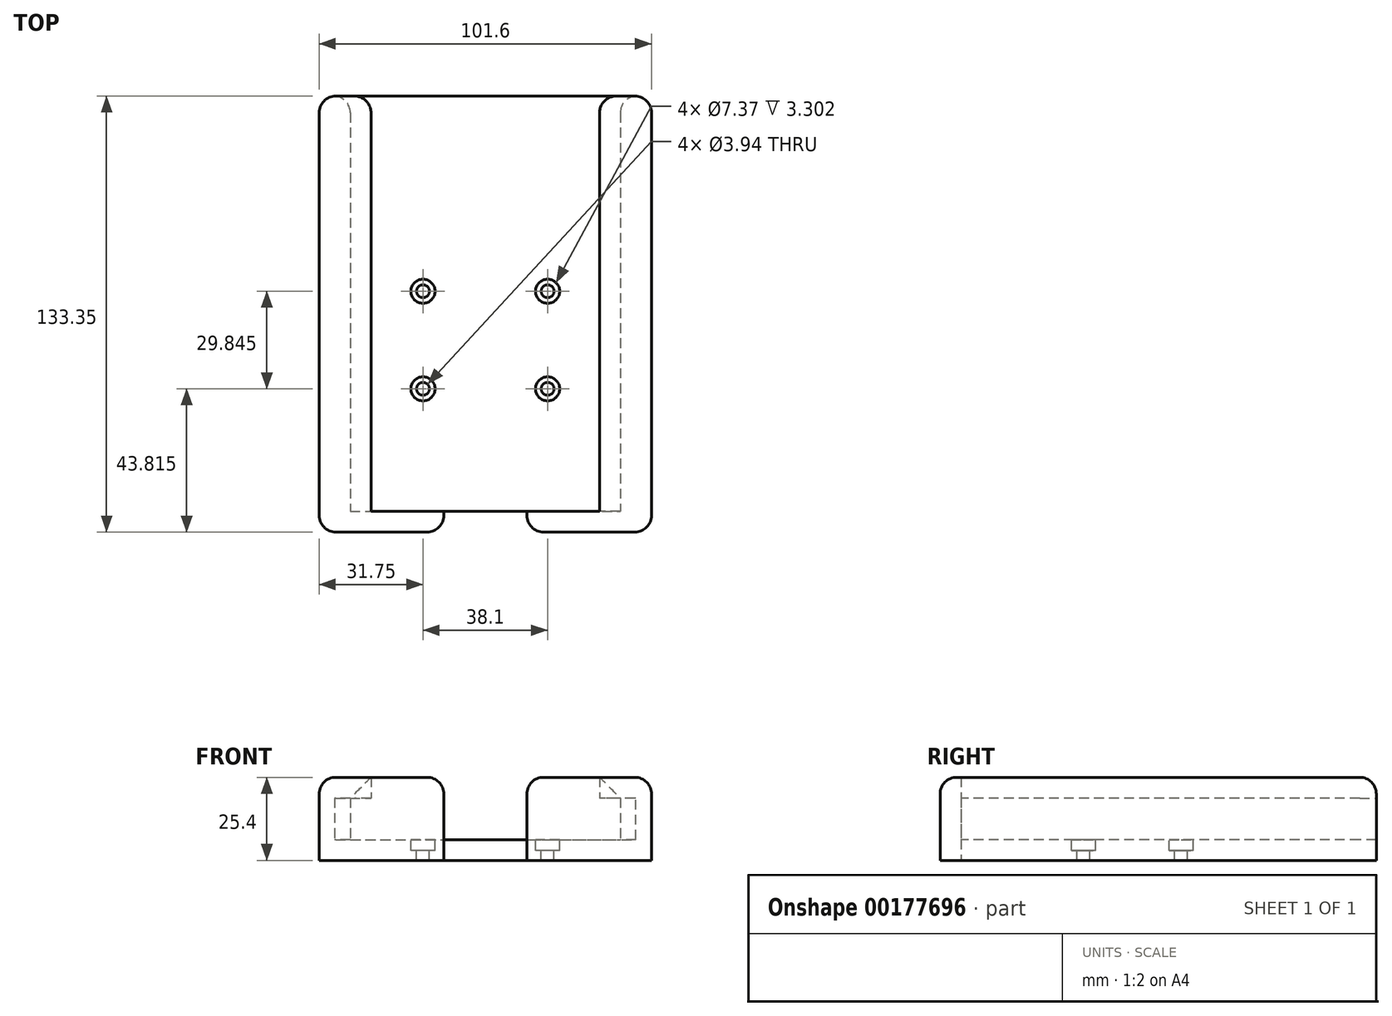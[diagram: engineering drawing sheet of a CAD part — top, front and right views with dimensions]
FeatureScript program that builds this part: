
annotation { "Feature Type Name" : "Feature", "Feature Type Description" : "" }
export const myFeature = defineFeature(function(context is Context, id is Id, definition is map)
    precondition{}
    {
        {
            var Q0;
            Q0=qCreatedBy(makeId("Top.planeOp"),FACE);
            var sketch = newSketch(context, id + "F0", { "sketchPlane" : qUnion([Q0])});
            skLineSegment(sketch, "E0.bottom", {"start": v(-50.8, 63.5) * mm, "end": v(50.8, 63.5) * mm});
            skLineSegment(sketch, "E0.top", {"start": v(-50.8, -63.5) * mm, "end": v(50.8, -63.5) * mm});
            skLineSegment(sketch, "E0.left", {"start": v(-50.8, 63.5) * mm, "end": v(-50.8, -63.5) * mm});
            skLineSegment(sketch, "E0.right", {"start": v(50.8, 63.5) * mm, "end": v(50.8, -63.5) * mm});
            skSolve(sketch);
        }
        {
            var Q0;
            Q0=makeQuery(id+"F0.imprint","IMPRINT",FACE,{"disambiguationData":[TD([[makeQuery(id+"F0.imprint","IMPRINT",EDGE,{"derivedFrom":sQuery(id+"F0.wireOp",EDGE,"E0.bottom")}),-1.0]])]});
            extrude(context, id + "F1", {"entities" : qUnion([Q0]), "depth" : 6.35 * mm});
        }
        {
            var Q0;
            Q0=makeQuery(id+"F1.opExtrude","CAP_FACE",FACE,{"disambiguationData":[OSD([sQuery(id+"F0.wireOp",EDGE,"E0.bottom"),sQuery(id+"F0.wireOp",EDGE,"E0.top"),sQuery(id+"F0.wireOp",EDGE,"E0.left"),sQuery(id+"F0.wireOp",EDGE,"E0.right")])],"isStart":false});
            var sketch = newSketch(context, id + "F2", { "sketchPlane" : qUnion([Q0])});
            skLineSegment(sketch, "E1.bottom", {"start": v(-50.8, 63.5) * mm, "end": v(-41.27, 63.5) * mm});
            skLineSegment(sketch, "E1.top", {"start": v(-50.8, -63.5) * mm, "end": v(-41.27, -63.5) * mm});
            skLineSegment(sketch, "E1.left", {"start": v(-50.8, 63.5) * mm, "end": v(-50.8, -63.5) * mm});
            skLineSegment(sketch, "E1.right", {"start": v(-41.27, 63.5) * mm, "end": v(-41.27, -63.5) * mm});
            skLineSegment(sketch, "E2.bottom", {"start": v(50.8, 63.5) * mm, "end": v(41.28, 63.5) * mm});
            skLineSegment(sketch, "E2.top", {"start": v(50.8, -63.5) * mm, "end": v(41.28, -63.5) * mm});
            skLineSegment(sketch, "E2.left", {"start": v(50.8, 63.5) * mm, "end": v(50.8, -63.5) * mm});
            skLineSegment(sketch, "E2.right", {"start": v(41.28, 63.5) * mm, "end": v(41.28, -63.5) * mm});
            skSolve(sketch);
        }
        {
            var Q0;
            Q0=makeQuery(id+"F2.imprint","IMPRINT",FACE,{"disambiguationData":[TD([[makeQuery(id+"F2.imprint","IMPRINT",EDGE,{"derivedFrom":sQuery(id+"F2.wireOp",EDGE,"E1.bottom")}),-1.0]])]});
            var Q1;
            Q1=makeQuery(id+"F2.imprint","IMPRINT",FACE,{"disambiguationData":[TD([[makeQuery(id+"F2.imprint","IMPRINT",EDGE,{"derivedFrom":sQuery(id+"F2.wireOp",EDGE,"E2.bottom")}),-1.0]])]});
            extrude(context, id + "F3", {"entities" : qUnion([Q0, Q1]), "operationType" : NewBodyOperationType.ADD, "depth" : 12.7 * mm});
        }
        {
            var Q0;
            Q0=makeQuery(id+"F3.opExtrude","CAP_FACE",FACE,{"disambiguationData":[OSD([sQuery(id+"F2.wireOp",EDGE,"E1.bottom"),sQuery(id+"F2.wireOp",EDGE,"E1.top"),sQuery(id+"F2.wireOp",EDGE,"E1.left"),sQuery(id+"F2.wireOp",EDGE,"E1.right")])],"isStart":false});
            var sketch = newSketch(context, id + "F4", { "sketchPlane" : qUnion([Q0])});
            skLineSegment(sketch, "E3.bottom", {"start": v(-50.8, 63.5) * mm, "end": v(-34.92, 63.5) * mm});
            skLineSegment(sketch, "E3.top", {"start": v(-50.8, -63.5) * mm, "end": v(-34.92, -63.5) * mm});
            skLineSegment(sketch, "E3.left", {"start": v(-50.8, 63.5) * mm, "end": v(-50.8, -63.5) * mm});
            skLineSegment(sketch, "E3.right", {"start": v(-34.92, 63.5) * mm, "end": v(-34.92, -63.5) * mm});
            skLineSegment(sketch, "E4.MirrorCS", {"start": v(50.8, 63.5) * mm, "end": v(34.92, 63.5) * mm});
            skLineSegment(sketch, "E5.MirrorCS", {"start": v(50.8, 63.5) * mm, "end": v(50.8, -63.5) * mm});
            skLineSegment(sketch, "E6.MirrorCS", {"start": v(34.92, 63.5) * mm, "end": v(34.92, -63.5) * mm});
            skLineSegment(sketch, "E7.MirrorCS", {"start": v(50.8, -63.5) * mm, "end": v(34.92, -63.5) * mm});
            skSolve(sketch);
        }
        {
            var Q0;
            {var subQ2=sQuery(id+"F4.wireOp",EDGE,"E3.right");Q0=makeQuery(id+"F4.imprint","IMPRINT",FACE,{"disambiguationData":[TD([[makeQuery(id+"F4.imprint","IMPRINT",EDGE,{"derivedFrom":subQ2}),-1.0]])]});}
            var Q1;
            {var subQ0=sQuery(id+"F4.wireOp",EDGE,"E3.left");Q1=makeQuery(id+"F4.imprint","IMPRINT",FACE,{"disambiguationData":[TD([[makeQuery(id+"F4.imprint","IMPRINT",EDGE,{"derivedFrom":subQ0}),1.0]])]});}
            var Q2;
            Q2=makeQuery(id+"F4.imprint","IMPRINT",FACE,{"disambiguationData":[TD([[makeQuery(id+"F4.imprint","IMPRINT",EDGE,{"derivedFrom":sQuery(id+"F4.wireOp",EDGE,"E4.MirrorCS")}),1.0]])]});
            extrude(context, id + "F5", {"entities" : qUnion([Q0, Q1, Q2]), "operationType" : NewBodyOperationType.ADD, "depth" : 6.35 * mm});
        }
        {
            var Q0;
            Q0=makeQuery(id+"F1.opExtrude","CAP_FACE",FACE,{"disambiguationData":[OSD([sQuery(id+"F0.wireOp",EDGE,"E0.bottom"),sQuery(id+"F0.wireOp",EDGE,"E0.top"),sQuery(id+"F0.wireOp",EDGE,"E0.left"),sQuery(id+"F0.wireOp",EDGE,"E0.right")])],"isStart":false});
            var sketch = newSketch(context, id + "F6", { "sketchPlane" : qUnion([Q0])});
            skLineSegment(sketch, "E8.bottom", {"start": v(-19.05, 3.81) * mm, "end": v(19.05, 3.81) * mm, "construction": true});
            skLineSegment(sketch, "E8.top", {"start": v(-19.05, -26.04) * mm, "end": v(19.05, -26.04) * mm, "construction": true});
            skLineSegment(sketch, "E8.left", {"start": v(-19.05, 3.81) * mm, "end": v(-19.05, -26.04) * mm, "construction": true});
            skLineSegment(sketch, "E8.right", {"start": v(19.05, 3.81) * mm, "end": v(19.05, -26.04) * mm, "construction": true});
            skCircle(sketch, "E9", {"center": v(-19.05, 3.81) * mm, "radius": 3.68 * mm});
            skCircle(sketch, "E10", {"center": v(19.05, 3.81) * mm, "radius": 3.68 * mm});
            skCircle(sketch, "E11", {"center": v(19.05, -26.04) * mm, "radius": 3.68 * mm});
            skCircle(sketch, "E12", {"center": v(-19.05, -26.04) * mm, "radius": 3.68 * mm});
            skSolve(sketch);
        }
        {
            var Q0;
            Q0=makeQuery(id+"F6.imprint","IMPRINT",FACE,{"disambiguationData":[TD([[makeQuery(id+"F6.imprint","IMPRINT",EDGE,{"derivedFrom":sQuery(id+"F6.wireOp",EDGE,"E9")}),1.0]])]});
            var Q1;
            Q1=makeQuery(id+"F6.imprint","IMPRINT",FACE,{"disambiguationData":[TD([[makeQuery(id+"F6.imprint","IMPRINT",EDGE,{"derivedFrom":sQuery(id+"F6.wireOp",EDGE,"E12")}),1.0]])]});
            var Q2;
            Q2=makeQuery(id+"F6.imprint","IMPRINT",FACE,{"disambiguationData":[TD([[makeQuery(id+"F6.imprint","IMPRINT",EDGE,{"derivedFrom":sQuery(id+"F6.wireOp",EDGE,"E11")}),1.0]])]});
            var Q3;
            Q3=makeQuery(id+"F6.imprint","IMPRINT",FACE,{"disambiguationData":[TD([[makeQuery(id+"F6.imprint","IMPRINT",EDGE,{"derivedFrom":sQuery(id+"F6.wireOp",EDGE,"E10")}),1.0]])]});
            extrude(context, id + "F7", {"entities" : qUnion([Q0, Q1, Q2, Q3]), "operationType" : NewBodyOperationType.REMOVE, "oppositeDirection" : true, "depth" : 3.3 * mm});
        }
        {
            var Q0;
            Q0=makeQuery(id+"F7.boolean.opBoolean","COPY",FACE,{"derivedFrom":makeQuery(id+"F7.opExtrude","CAP_FACE",FACE,{"disambiguationData":[OSD([sQuery(id+"F6.wireOp",EDGE,"E9")])],"isStart":false})});
            var sketch = newSketch(context, id + "F8", { "sketchPlane" : qUnion([Q0])});
            skCircle(sketch, "E13.0", {"center": v(-19.05, 3.81) * mm, "radius": 3.68 * mm});
            skCircle(sketch, "E14.0", {"center": v(19.05, 3.81) * mm, "radius": 3.68 * mm});
            skCircle(sketch, "E15.0", {"center": v(19.05, -26.04) * mm, "radius": 3.68 * mm});
            skCircle(sketch, "E16.0", {"center": v(-19.05, -26.04) * mm, "radius": 3.68 * mm});
            skCircle(sketch, "E17", {"center": v(-19.05, 3.81) * mm, "radius": 1.97 * mm});
            skCircle(sketch, "E18", {"center": v(19.05, 3.81) * mm, "radius": 1.97 * mm});
            skCircle(sketch, "E19", {"center": v(19.05, -26.04) * mm, "radius": 1.97 * mm});
            skCircle(sketch, "E20", {"center": v(-19.05, -26.04) * mm, "radius": 1.97 * mm});
            skSolve(sketch);
        }
        {
            var Q0;
            Q0=makeQuery(id+"F8.imprint","IMPRINT",FACE,{"disambiguationData":[TD([[makeQuery(id+"F8.imprint","IMPRINT",EDGE,{"derivedFrom":sQuery(id+"F8.wireOp",EDGE,"E17")}),1.0]])]});
            var Q1;
            Q1=makeQuery(id+"F8.imprint","IMPRINT",FACE,{"disambiguationData":[TD([[makeQuery(id+"F8.imprint","IMPRINT",EDGE,{"derivedFrom":sQuery(id+"F8.wireOp",EDGE,"E18")}),1.0]])]});
            var Q2;
            Q2=makeQuery(id+"F8.imprint","IMPRINT",FACE,{"disambiguationData":[TD([[makeQuery(id+"F8.imprint","IMPRINT",EDGE,{"derivedFrom":sQuery(id+"F8.wireOp",EDGE,"E20")}),1.0]])]});
            var Q3;
            Q3=makeQuery(id+"F8.imprint","IMPRINT",FACE,{"disambiguationData":[TD([[makeQuery(id+"F8.imprint","IMPRINT",EDGE,{"derivedFrom":sQuery(id+"F8.wireOp",EDGE,"E19")}),1.0]])]});
            extrude(context, id + "F9", {"entities" : qUnion([Q0, Q1, Q2, Q3]), "operationType" : NewBodyOperationType.REMOVE, "oppositeDirection" : true, "depth" : 25.4 * mm});
        }
        {
            var Q0;
            Q0=makeQuery(id+"F5.boolean.opBoolean","MERGE",FACE,{"derivedFrom":[makeQuery(id+"F3.boolean.opBoolean","MERGE",FACE,{"derivedFrom":[makeQuery(id+"F1.opExtrude","SWEPT_FACE",FACE,{"disambiguationData":[OSD([sQuery(id+"F0.wireOp",EDGE,"E0.top")])]}),makeQuery(id+"F3.opExtrude","SWEPT_FACE",FACE,{"disambiguationData":[OSD([sQuery(id+"F2.wireOp",EDGE,"E1.top")])]}),makeQuery(id+"F3.opExtrude","SWEPT_FACE",FACE,{"disambiguationData":[OSD([sQuery(id+"F2.wireOp",EDGE,"E2.top")])]})]}),makeQuery(id+"F5.opExtrude","SWEPT_FACE",FACE,{"disambiguationData":[OSD([sQuery(id+"F4.wireOp",EDGE,"E3.top")])]}),makeQuery(id+"F5.opExtrude","SWEPT_FACE",FACE,{"disambiguationData":[OSD([sQuery(id+"F4.wireOp",EDGE,"E7.MirrorCS")])]})]});
            var sketch = newSketch(context, id + "F10", { "sketchPlane" : qUnion([Q0])});
            skLineSegment(sketch, "E21.bottom", {"start": v(-50.8, 25.4) * mm, "end": v(50.8, 25.4) * mm});
            skLineSegment(sketch, "E21.top", {"start": v(-50.8, 0) * mm, "end": v(50.8, 0) * mm});
            skLineSegment(sketch, "E21.left", {"start": v(-50.8, 25.4) * mm, "end": v(-50.8, 0) * mm});
            skLineSegment(sketch, "E21.right", {"start": v(50.8, 25.4) * mm, "end": v(50.8, 0) * mm});
            skLineSegment(sketch, "E22.bottom", {"start": v(-12.7, 25.4) * mm, "end": v(12.7, 25.4) * mm});
            skLineSegment(sketch, "E22.top", {"start": v(-12.7, 0) * mm, "end": v(12.7, 0) * mm});
            skLineSegment(sketch, "E22.left", {"start": v(-12.7, 25.4) * mm, "end": v(-12.7, 0) * mm});
            skLineSegment(sketch, "E22.right", {"start": v(12.7, 25.4) * mm, "end": v(12.7, 0) * mm});
            skSolve(sketch);
        }
        {
            var Q0;
            {var subQ0=sQuery(id+"F10.wireOp",EDGE,"E21.left");Q0=makeQuery(id+"F10.imprint","IMPRINT",FACE,{"disambiguationData":[TD([[makeQuery(id+"F10.imprint","IMPRINT",EDGE,{"derivedFrom":subQ0}),1.0]])]});}
            var Q1;
            {var subQ0=sQuery(id+"F4.wireOp",EDGE,"E3.top");Q1=makeQuery(id+"F10.imprint","IMPRINT",FACE,{"disambiguationData":[TD([[makeQuery(id+"F10.imprint","IMPRINT",EDGE,{"derivedFrom":makeQuery(id+"F5.opExtrude","CAP_EDGE",EDGE,{"disambiguationData":[OSD([subQ0])],"isStart":true})}),-1.0]])]});}
            var Q2;
            {var subQ0=sQuery(id+"F4.wireOp",EDGE,"E7.MirrorCS");Q2=makeQuery(id+"F10.imprint","IMPRINT",FACE,{"disambiguationData":[TD([[makeQuery(id+"F10.imprint","IMPRINT",EDGE,{"derivedFrom":makeQuery(id+"F5.opExtrude","CAP_EDGE",EDGE,{"disambiguationData":[OSD([subQ0])],"isStart":true})}),1.0]])]});}
            var Q3;
            {var subQ6=sQuery(id+"F10.wireOp",EDGE,"E21.right");Q3=makeQuery(id+"F10.imprint","IMPRINT",FACE,{"disambiguationData":[TD([[makeQuery(id+"F10.imprint","IMPRINT",EDGE,{"derivedFrom":subQ6}),-1.0]])]});}
            var Q4;
            {var subQ0=sQuery(id+"F10.wireOp",EDGE,"E22.top");Q4=makeQuery(id+"F10.imprint","IMPRINT",FACE,{"disambiguationData":[TD([[makeQuery(id+"F10.imprint","IMPRINT",EDGE,{"derivedFrom":subQ0}),1.0]])]});}
            extrude(context, id + "F11", {"entities" : qUnion([Q0, Q1, Q2, Q3, Q4]), "operationType" : NewBodyOperationType.ADD, "depth" : 6.35 * mm});
        }
        {
            var Q0;
            Q0=makeQuery(id+"F11.boolean.opBoolean","MERGE",EDGE,{"derivedFrom":[makeQuery(id+"F5.opExtrude","CAP_EDGE",EDGE,{"disambiguationData":[OSD([sQuery(id+"F4.wireOp",EDGE,"E3.left")])],"isStart":false}),makeQuery(id+"F11.opExtrude","SWEPT_EDGE",EDGE,{"disambiguationData":[OSD([sQuery(id+"F10.wireOp",EDGE,"E21.bottom"),sQuery(id+"F10.wireOp",EDGE,"E21.left")])]})]});
            var Q1;
            Q1=makeQuery(id+"F11.boolean.opBoolean","MERGE",EDGE,{"derivedFrom":[makeQuery(id+"F5.opExtrude","CAP_EDGE",EDGE,{"disambiguationData":[OSD([sQuery(id+"F4.wireOp",EDGE,"E5.MirrorCS")])],"isStart":false}),makeQuery(id+"F11.opExtrude","SWEPT_EDGE",EDGE,{"disambiguationData":[OSD([sQuery(id+"F10.wireOp",EDGE,"E21.bottom"),sQuery(id+"F10.wireOp",EDGE,"E21.right")])]})]});
            fillet(context, id + "F12", {"entities" : qUnion([Q0, Q1]), "radius" : 5.08 * mm, "tangentPropagation" : true, "allowEdgeOverflow" : false});
        }
        {
            var Q0;
            Q0=makeQuery(id+"F5.opExtrude","SWEPT_EDGE",EDGE,{"disambiguationData":[OSD([sQuery(id+"F4.wireOp",EDGE,"E3.bottom"),sQuery(id+"F4.wireOp",EDGE,"E3.right")])]});
            var Q1;
            Q1=makeQuery(id+"F5.opExtrude","SWEPT_EDGE",EDGE,{"disambiguationData":[OSD([sQuery(id+"F4.wireOp",EDGE,"E4.MirrorCS"),sQuery(id+"F4.wireOp",EDGE,"E6.MirrorCS")])]});
            var Q2;
            Q2=makeQuery(id+"F5.boolean.opBoolean","MERGE",EDGE,{"derivedFrom":[makeQuery(id+"F3.boolean.opBoolean","MERGE",EDGE,{"derivedFrom":[makeQuery(id+"F1.opExtrude","SWEPT_EDGE",EDGE,{"disambiguationData":[OSD([sQuery(id+"F0.wireOp",EDGE,"E0.bottom"),sQuery(id+"F0.wireOp",EDGE,"E0.left")])]}),makeQuery(id+"F3.opExtrude","SWEPT_EDGE",EDGE,{"disambiguationData":[OSD([sQuery(id+"F2.wireOp",EDGE,"E1.bottom"),sQuery(id+"F2.wireOp",EDGE,"E1.left")])]})]}),makeQuery(id+"F5.opExtrude","SWEPT_EDGE",EDGE,{"disambiguationData":[OSD([sQuery(id+"F4.wireOp",EDGE,"E3.bottom"),sQuery(id+"F4.wireOp",EDGE,"E3.left")])]})]});
            var Q3;
            Q3=makeQuery(id+"F5.boolean.opBoolean","MERGE",EDGE,{"derivedFrom":[makeQuery(id+"F3.boolean.opBoolean","MERGE",EDGE,{"derivedFrom":[makeQuery(id+"F1.opExtrude","SWEPT_EDGE",EDGE,{"disambiguationData":[OSD([sQuery(id+"F0.wireOp",EDGE,"E0.bottom"),sQuery(id+"F0.wireOp",EDGE,"E0.right")])]}),makeQuery(id+"F3.opExtrude","SWEPT_EDGE",EDGE,{"disambiguationData":[OSD([sQuery(id+"F2.wireOp",EDGE,"E2.bottom"),sQuery(id+"F2.wireOp",EDGE,"E2.left")])]})]}),makeQuery(id+"F5.opExtrude","SWEPT_EDGE",EDGE,{"disambiguationData":[OSD([sQuery(id+"F4.wireOp",EDGE,"E4.MirrorCS"),sQuery(id+"F4.wireOp",EDGE,"E5.MirrorCS")])]})]});
            var Q4;
            Q4=makeQuery(id+"F11.opExtrude","CAP_EDGE",EDGE,{"disambiguationData":[OSD([sQuery(id+"F10.wireOp",EDGE,"E21.left")])],"isStart":false});
            var Q5;
            Q5=makeQuery(id+"F11.opExtrude","CAP_EDGE",EDGE,{"disambiguationData":[OSD([sQuery(id+"F10.wireOp",EDGE,"E21.right")])],"isStart":false});
            var Q6;
            Q6=makeQuery(id+"F5.opExtrude","SWEPT_EDGE",EDGE,{"disambiguationData":[OSD([sQuery(id+"F4.wireOp",EDGE,"E3.top"),sQuery(id+"F4.wireOp",EDGE,"E3.right")])]});
            var Q7;
            Q7=makeQuery(id+"F5.opExtrude","SWEPT_EDGE",EDGE,{"disambiguationData":[OSD([sQuery(id+"F4.wireOp",EDGE,"E6.MirrorCS"),sQuery(id+"F4.wireOp",EDGE,"E7.MirrorCS")])]});
            fillet(context, id + "F13", {"entities" : qUnion([Q0, Q1, Q2, Q3, Q4, Q5, Q6, Q7]), "radius" : 5.08 * mm, "tangentPropagation" : true, "allowEdgeOverflow" : false});
        }
        {
            var Q0;
            Q0=makeQuery(id+"F3.opExtrude","SWEPT_EDGE",EDGE,{"disambiguationData":[OSD([sQuery(id+"F0.wireOp",EDGE,"E0.bottom"),sQuery(id+"F2.wireOp",EDGE,"E1.bottom"),sQuery(id+"F2.wireOp",EDGE,"E1.right")])]});
            var Q1;
            Q1=makeQuery(id+"F3.opExtrude","SWEPT_EDGE",EDGE,{"disambiguationData":[OSD([sQuery(id+"F0.wireOp",EDGE,"E0.bottom"),sQuery(id+"F2.wireOp",EDGE,"E2.bottom"),sQuery(id+"F2.wireOp",EDGE,"E2.right")])]});
            var Q2;
            Q2=makeQuery(id+"F3.opExtrude","SWEPT_EDGE",EDGE,{"disambiguationData":[OSD([sQuery(id+"F0.wireOp",EDGE,"E0.top"),sQuery(id+"F2.wireOp",EDGE,"E1.top"),sQuery(id+"F2.wireOp",EDGE,"E1.right")])]});
            var Q3;
            Q3=makeQuery(id+"F3.opExtrude","SWEPT_EDGE",EDGE,{"disambiguationData":[OSD([sQuery(id+"F0.wireOp",EDGE,"E0.top"),sQuery(id+"F2.wireOp",EDGE,"E2.top"),sQuery(id+"F2.wireOp",EDGE,"E2.right")])]});
            fillet(context, id + "F14", {"entities" : qUnion([Q0, Q1, Q2, Q3]), "radius" : 5.08 * mm, "tangentPropagation" : true, "allowEdgeOverflow" : false});
        }
        {
            var Q0;
            Q0=makeQuery(id+"F11.opExtrude","SWEPT_EDGE",EDGE,{"disambiguationData":[OSD([sQuery(id+"F10.wireOp",EDGE,"E21.bottom"),sQuery(id+"F10.wireOp",EDGE,"E22.bottom"),sQuery(id+"F10.wireOp",EDGE,"E22.left")])]});
            var Q1;
            Q1=makeQuery(id+"F11.opExtrude","SWEPT_EDGE",EDGE,{"disambiguationData":[OSD([sQuery(id+"F10.wireOp",EDGE,"E21.bottom"),sQuery(id+"F10.wireOp",EDGE,"E22.bottom"),sQuery(id+"F10.wireOp",EDGE,"E22.right")])]});
            fillet(context, id + "F15", {"entities" : qUnion([Q0, Q1]), "radius" : 5.08 * mm, "tangentPropagation" : true, "allowEdgeOverflow" : false});
        }
    });
